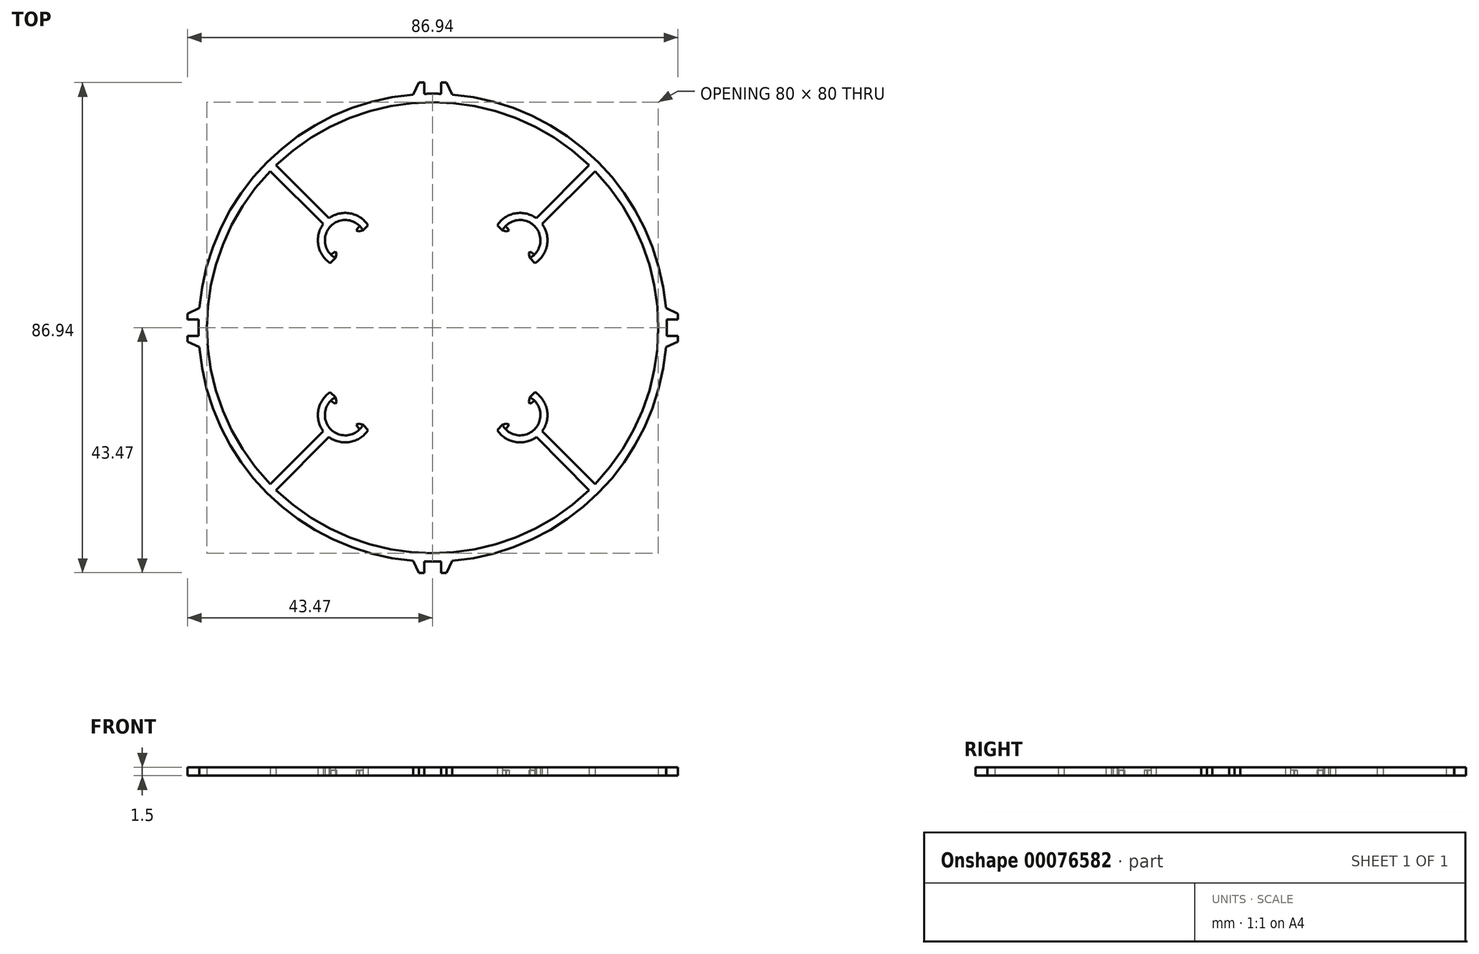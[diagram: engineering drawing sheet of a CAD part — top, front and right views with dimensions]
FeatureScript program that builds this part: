
annotation { "Feature Type Name" : "Feature", "Feature Type Description" : "" }
export const myFeature = defineFeature(function(context is Context, id is Id, definition is map)
    precondition{}
    {
        {
            var Q0;
            Q0=qCreatedBy(makeId("Top.planeOp"),FACE);
            var sketch = newSketch(context, id + "F0", { "sketchPlane" : qUnion([Q0])});
            skLineSegment(sketch, "E0.bottom", {"start": v(-15.5, 15.5) * mm, "end": v(15.5, 15.5) * mm});
            skLineSegment(sketch, "E0.top", {"start": v(-15.5, -15.5) * mm, "end": v(15.5, -15.5) * mm});
            skLineSegment(sketch, "E0.left", {"start": v(-15.5, 15.5) * mm, "end": v(-15.5, -15.5) * mm});
            skLineSegment(sketch, "E0.right", {"start": v(15.5, 15.5) * mm, "end": v(15.5, -15.5) * mm});
            skPoint(sketch, "E0.middle", {"position": v(0, 0) * mm});
            skCircle(sketch, "E1", {"center": v(-15.5, 15.5) * mm, "radius": 15 * mm});
            skCircle(sketch, "E2", {"center": v(15.5, 15.5) * mm, "radius": 15 * mm});
            skCircle(sketch, "E3", {"center": v(-15.5, -15.5) * mm, "radius": 15 * mm});
            skCircle(sketch, "E4", {"center": v(15.5, -15.5) * mm, "radius": 15 * mm});
            skLineSegment(sketch, "E5.bottom", {"start": v(-10, 10) * mm, "end": v(10, 10) * mm});
            skLineSegment(sketch, "E5.top", {"start": v(-10, -10) * mm, "end": v(10, -10) * mm});
            skLineSegment(sketch, "E5.left", {"start": v(-10, 10) * mm, "end": v(-10, -10) * mm});
            skLineSegment(sketch, "E5.right", {"start": v(10, 10) * mm, "end": v(10, -10) * mm});
            skCircle(sketch, "E6", {"center": v(-15.5, 15.5) * mm, "radius": 4.5 * mm});
            skCircle(sketch, "E7", {"center": v(-15.5, 15.5) * mm, "radius": 3.5 * mm});
            skCircle(sketch, "E8", {"center": v(15.5, 15.5) * mm, "radius": 3.5 * mm});
            skCircle(sketch, "E9", {"center": v(15.5, 15.5) * mm, "radius": 4.5 * mm});
            skCircle(sketch, "E10", {"center": v(15.5, -15.5) * mm, "radius": 4.5 * mm});
            skCircle(sketch, "E11", {"center": v(15.5, -15.5) * mm, "radius": 3.5 * mm});
            skCircle(sketch, "E12", {"center": v(-15.5, -15.5) * mm, "radius": 3.5 * mm});
            skCircle(sketch, "E13", {"center": v(-15.5, -15.5) * mm, "radius": 4.5 * mm});
            skLineSegment(sketch, "E14.bottom", {"start": v(-15.5, 15.5) * mm, "end": v(-10.5, 15.5) * mm});
            skLineSegment(sketch, "E14.left", {"start": v(-15.5, 15.5) * mm, "end": v(-15.5, 20.5) * mm});
            skLineSegment(sketch, "E15", {"start": v(-12.32, 18.68) * mm, "end": v(-18.68, 12.32) * mm});
            skLineSegment(sketch, "E16", {"start": v(-17.9, 11.7) * mm, "end": v(-11.7, 17.9) * mm});
            skSolve(sketch);
        }
        {
            var Q0;
            {var subQ1=sQuery(id+"F0.wireOp",EDGE,"E0.bottom");var subQ5=sQuery(id+"F0.wireOp",EDGE,"E14.bottom");var subQ6=makeQuery(id+"F0.imprint","INTERSECT",VERTEX,{"derivedFrom":[subQ1,subQ5]});Q0=makeQuery(id+"F0.imprint","IMPRINT",FACE,{"disambiguationData":[TD([[makeQuery(id+"F0.imprint","IMPRINT",EDGE,{"disambiguationData":[TD([[subQ6,-1.0]])],"derivedFrom":subQ1}),1.0]])]});}
            var sketch = newSketch(context, id + "F1", { "sketchPlane" : qUnion([Q0])});
            skCircle(sketch, "E17", {"center": v(0, 0) * mm, "radius": 41.5 * mm});
            skLineSegment(sketch, "E18", {"start": v(-17.05, 13.08) * mm, "end": v(-17.24, 13.54) * mm});
            skLineSegment(sketch, "E19", {"start": v(-17.24, 13.54) * mm, "end": v(-18.05, 12.95) * mm});
            skLineSegment(sketch, "E20", {"start": v(-18.39, 19.4) * mm, "end": v(-27.75, 28.8) * mm});
            skLineSegment(sketch, "E21", {"start": v(-19.4, 18.39) * mm, "end": v(-28.8, 27.75) * mm});
            skLineSegment(sketch, "E22", {"start": v(-17.25, 12.35) * mm, "end": v(-17.05, 13.08) * mm});
            skArc(sketch, "E23", {"start": v(-11.44, 18.16) * mm, "mid": v(-14.65, 20.27) * mm, "end": v(-18.39, 19.4) * mm});
            skArc(sketch, "E24", {"start": v(-12.95, 18.05) * mm, "mid": v(-18.05, 18.05) * mm, "end": v(-18.05, 12.95) * mm});
            skLineSegment(sketch, "E25.0", {"start": v(-17.9, 11.7) * mm, "end": v(-11.7, 17.9) * mm, "construction": true});
            skLineSegment(sketch, "E26", {"start": v(-12.95, 18.05) * mm, "end": v(-13.54, 17.24) * mm});
            skLineSegment(sketch, "E27", {"start": v(-13.54, 17.24) * mm, "end": v(-13.08, 17.05) * mm});
            skLineSegment(sketch, "E28", {"start": v(-13.08, 17.05) * mm, "end": v(-12.35, 17.25) * mm});
            skLineSegment(sketch, "E29", {"start": v(-12.35, 17.25) * mm, "end": v(-11.7, 17.9) * mm, "construction": true});
            skArc(sketch, "E30", {"start": v(-28.8, 27.75) * mm, "mid": v(-40, 0) * mm, "end": v(-28.8, -27.75) * mm});
            skLineSegment(sketch, "E31", {"start": v(-12.35, 17.25) * mm, "end": v(-11.44, 18.16) * mm});
            skLineSegment(sketch, "E32", {"start": v(-18.16, 11.44) * mm, "end": v(-17.25, 12.35) * mm});
            skArc(sketch, "E33.trimOffspring", {"start": v(-19.4, 18.39) * mm, "mid": v(-20.27, 14.65) * mm, "end": v(-18.16, 11.44) * mm});
            skArc(sketch, "E34.1.0", {"start": v(-18.39, -19.4) * mm, "mid": v(-14.65, -20.27) * mm, "end": v(-11.44, -18.16) * mm});
            skLineSegment(sketch, "E34.1.1", {"start": v(-19.4, -18.39) * mm, "end": v(-28.8, -27.75) * mm});
            skArc(sketch, "E34.1.2", {"start": v(-18.05, -12.95) * mm, "mid": v(-18.05, -18.05) * mm, "end": v(-12.95, -18.05) * mm});
            skLineSegment(sketch, "E34.1.3", {"start": v(-11.7, -17.9) * mm, "end": v(-17.9, -11.7) * mm, "construction": true});
            skArc(sketch, "E34.1.4", {"start": v(-18.16, -11.44) * mm, "mid": v(-20.27, -14.65) * mm, "end": v(-19.4, -18.39) * mm});
            skLineSegment(sketch, "E34.1.5", {"start": v(-18.39, -19.4) * mm, "end": v(-27.75, -28.8) * mm});
            skLineSegment(sketch, "E34.1.6", {"start": v(-18.05, -12.95) * mm, "end": v(-17.24, -13.54) * mm});
            skLineSegment(sketch, "E34.1.7", {"start": v(-13.54, -17.24) * mm, "end": v(-12.95, -18.05) * mm});
            skLineSegment(sketch, "E34.1.8", {"start": v(-17.05, -13.08) * mm, "end": v(-17.25, -12.35) * mm});
            skLineSegment(sketch, "E34.1.9", {"start": v(-17.24, -13.54) * mm, "end": v(-17.05, -13.08) * mm});
            skLineSegment(sketch, "E34.1.10", {"start": v(-11.44, -18.16) * mm, "end": v(-12.35, -17.25) * mm});
            skLineSegment(sketch, "E34.1.11", {"start": v(-12.35, -17.25) * mm, "end": v(-13.08, -17.05) * mm});
            skLineSegment(sketch, "E34.1.12", {"start": v(-17.25, -12.35) * mm, "end": v(-18.16, -11.44) * mm});
            skLineSegment(sketch, "E34.1.13", {"start": v(-13.08, -17.05) * mm, "end": v(-13.54, -17.24) * mm});
            skLineSegment(sketch, "E34.1.14", {"start": v(-17.25, -12.35) * mm, "end": v(-17.9, -11.7) * mm, "construction": true});
            skArc(sketch, "E34.2.0", {"start": v(19.4, -18.39) * mm, "mid": v(20.27, -14.65) * mm, "end": v(18.16, -11.44) * mm});
            skLineSegment(sketch, "E34.2.1", {"start": v(18.39, -19.4) * mm, "end": v(27.75, -28.8) * mm});
            skArc(sketch, "E34.2.2", {"start": v(12.95, -18.05) * mm, "mid": v(18.05, -18.05) * mm, "end": v(18.05, -12.95) * mm});
            skLineSegment(sketch, "E34.2.3", {"start": v(17.9, -11.7) * mm, "end": v(11.7, -17.9) * mm, "construction": true});
            skArc(sketch, "E34.2.4", {"start": v(11.44, -18.16) * mm, "mid": v(14.65, -20.27) * mm, "end": v(18.39, -19.4) * mm});
            skLineSegment(sketch, "E34.2.5", {"start": v(19.4, -18.39) * mm, "end": v(28.8, -27.75) * mm});
            skLineSegment(sketch, "E34.2.6", {"start": v(12.95, -18.05) * mm, "end": v(13.54, -17.24) * mm});
            skLineSegment(sketch, "E34.2.7", {"start": v(17.24, -13.54) * mm, "end": v(18.05, -12.95) * mm});
            skLineSegment(sketch, "E34.2.8", {"start": v(13.08, -17.05) * mm, "end": v(12.35, -17.25) * mm});
            skLineSegment(sketch, "E34.2.9", {"start": v(13.54, -17.24) * mm, "end": v(13.08, -17.05) * mm});
            skLineSegment(sketch, "E34.2.10", {"start": v(18.16, -11.44) * mm, "end": v(17.25, -12.35) * mm});
            skLineSegment(sketch, "E34.2.11", {"start": v(17.25, -12.35) * mm, "end": v(17.05, -13.08) * mm});
            skLineSegment(sketch, "E34.2.12", {"start": v(12.35, -17.25) * mm, "end": v(11.44, -18.16) * mm});
            skLineSegment(sketch, "E34.2.13", {"start": v(17.05, -13.08) * mm, "end": v(17.24, -13.54) * mm});
            skLineSegment(sketch, "E34.2.14", {"start": v(12.35, -17.25) * mm, "end": v(11.7, -17.9) * mm, "construction": true});
            skArc(sketch, "E34.3.0", {"start": v(18.39, 19.4) * mm, "mid": v(14.65, 20.27) * mm, "end": v(11.44, 18.16) * mm});
            skLineSegment(sketch, "E34.3.1", {"start": v(19.4, 18.39) * mm, "end": v(28.8, 27.75) * mm});
            skArc(sketch, "E34.3.2", {"start": v(18.05, 12.95) * mm, "mid": v(18.05, 18.05) * mm, "end": v(12.95, 18.05) * mm});
            skLineSegment(sketch, "E34.3.3", {"start": v(11.7, 17.9) * mm, "end": v(17.9, 11.7) * mm, "construction": true});
            skArc(sketch, "E34.3.4", {"start": v(18.16, 11.44) * mm, "mid": v(20.27, 14.65) * mm, "end": v(19.4, 18.39) * mm});
            skLineSegment(sketch, "E34.3.5", {"start": v(18.39, 19.4) * mm, "end": v(27.75, 28.8) * mm});
            skLineSegment(sketch, "E34.3.6", {"start": v(18.05, 12.95) * mm, "end": v(17.24, 13.54) * mm});
            skLineSegment(sketch, "E34.3.7", {"start": v(13.54, 17.24) * mm, "end": v(12.95, 18.05) * mm});
            skLineSegment(sketch, "E34.3.8", {"start": v(17.05, 13.08) * mm, "end": v(17.25, 12.35) * mm});
            skLineSegment(sketch, "E34.3.9", {"start": v(17.24, 13.54) * mm, "end": v(17.05, 13.08) * mm});
            skLineSegment(sketch, "E34.3.10", {"start": v(11.44, 18.16) * mm, "end": v(12.35, 17.25) * mm});
            skLineSegment(sketch, "E34.3.11", {"start": v(12.35, 17.25) * mm, "end": v(13.08, 17.05) * mm});
            skLineSegment(sketch, "E34.3.12", {"start": v(17.25, 12.35) * mm, "end": v(18.16, 11.44) * mm});
            skLineSegment(sketch, "E34.3.13", {"start": v(13.08, 17.05) * mm, "end": v(13.54, 17.24) * mm});
            skLineSegment(sketch, "E34.3.14", {"start": v(17.25, 12.35) * mm, "end": v(17.9, 11.7) * mm, "construction": true});
            skArc(sketch, "E35.trimOffspring", {"start": v(27.75, 28.8) * mm, "mid": v(0, 40) * mm, "end": v(-27.75, 28.8) * mm});
            skArc(sketch, "E36.trimOffspring", {"start": v(28.8, -27.75) * mm, "mid": v(40, 0) * mm, "end": v(28.8, 27.75) * mm});
            skArc(sketch, "E37.trimOffspring", {"start": v(-27.75, -28.8) * mm, "mid": v(0, -40) * mm, "end": v(27.75, -28.8) * mm});
            skSolve(sketch);
        }
        {
            var Q0;
            Q0=qCreatedBy(makeId("Top.planeOp"),FACE);
            var sketch = newSketch(context, id + "F2", { "sketchPlane" : qUnion([Q0])});
            skLineSegment(sketch, "E38", {"start": v(-1.47, 43.47) * mm, "end": v(-2.47, 43.47) * mm});
            skLineSegment(sketch, "E39", {"start": v(-2.47, 43.47) * mm, "end": v(-3.46, 41.36) * mm});
            skLineSegment(sketch, "E40.MirrorCS", {"start": v(1.47, 43.47) * mm, "end": v(2.47, 43.47) * mm});
            skLineSegment(sketch, "E41.MirrorCS", {"start": v(2.47, 43.47) * mm, "end": v(3.46, 41.36) * mm});
            skLineSegment(sketch, "E42", {"start": v(-1.47, 43.47) * mm, "end": v(-1.47, 41.47) * mm});
            skLineSegment(sketch, "E43", {"start": v(1.47, 43.47) * mm, "end": v(1.47, 41.47) * mm});
            skLineSegment(sketch, "E44.1.0", {"start": v(-43.47, 1.47) * mm, "end": v(-43.47, 2.47) * mm});
            skLineSegment(sketch, "E44.1.1", {"start": v(-43.47, -1.47) * mm, "end": v(-43.47, -2.47) * mm});
            skLineSegment(sketch, "E44.1.2", {"start": v(-43.47, 2.47) * mm, "end": v(-41.36, 3.46) * mm});
            skLineSegment(sketch, "E44.1.3", {"start": v(-43.47, -2.47) * mm, "end": v(-41.36, -3.46) * mm});
            skLineSegment(sketch, "E44.1.4", {"start": v(-43.47, 1.47) * mm, "end": v(-41.47, 1.47) * mm});
            skLineSegment(sketch, "E44.1.5", {"start": v(-43.47, -1.47) * mm, "end": v(-41.47, -1.47) * mm});
            skLineSegment(sketch, "E44.2.0", {"start": v(-1.47, -43.47) * mm, "end": v(-2.47, -43.47) * mm});
            skLineSegment(sketch, "E44.2.1", {"start": v(1.47, -43.47) * mm, "end": v(2.47, -43.47) * mm});
            skLineSegment(sketch, "E44.2.2", {"start": v(-2.47, -43.47) * mm, "end": v(-3.46, -41.36) * mm});
            skLineSegment(sketch, "E44.2.3", {"start": v(2.47, -43.47) * mm, "end": v(3.46, -41.36) * mm});
            skLineSegment(sketch, "E44.2.4", {"start": v(-1.47, -43.47) * mm, "end": v(-1.47, -41.47) * mm});
            skLineSegment(sketch, "E44.2.5", {"start": v(1.47, -43.47) * mm, "end": v(1.47, -41.47) * mm});
            skLineSegment(sketch, "E44.3.0", {"start": v(43.47, -1.47) * mm, "end": v(43.47, -2.47) * mm});
            skLineSegment(sketch, "E44.3.1", {"start": v(43.47, 1.47) * mm, "end": v(43.47, 2.47) * mm});
            skLineSegment(sketch, "E44.3.2", {"start": v(43.47, -2.47) * mm, "end": v(41.36, -3.46) * mm});
            skLineSegment(sketch, "E44.3.3", {"start": v(43.47, 2.47) * mm, "end": v(41.36, 3.46) * mm});
            skLineSegment(sketch, "E44.3.4", {"start": v(43.47, -1.47) * mm, "end": v(41.47, -1.47) * mm});
            skLineSegment(sketch, "E44.3.5", {"start": v(43.47, 1.47) * mm, "end": v(41.47, 1.47) * mm});
            skPoint(sketch, "E44.center", {"position": v(0, 0) * mm});
            skLineSegment(sketch, "E45", {"start": v(-41.47, 1.47) * mm, "end": v(-41.36, 3.46) * mm});
            skLineSegment(sketch, "E46", {"start": v(-41.36, -3.46) * mm, "end": v(-41.47, -1.47) * mm});
            skLineSegment(sketch, "E47", {"start": v(-3.46, 41.36) * mm, "end": v(-1.47, 41.47) * mm});
            skLineSegment(sketch, "E48", {"start": v(1.47, 41.47) * mm, "end": v(3.46, 41.36) * mm});
            skLineSegment(sketch, "E49", {"start": v(41.36, 3.46) * mm, "end": v(41.47, 1.47) * mm});
            skLineSegment(sketch, "E50", {"start": v(41.47, -1.47) * mm, "end": v(41.36, -3.46) * mm});
            skLineSegment(sketch, "E51", {"start": v(1.47, -41.47) * mm, "end": v(3.46, -41.36) * mm});
            skLineSegment(sketch, "E52", {"start": v(-1.47, -41.47) * mm, "end": v(-3.46, -41.36) * mm});
            skSolve(sketch);
        }
        {
            var Q0;
            Q0 = qSketchRegion(id + "F1", true);
            extrude(context, id + "F3", {"entities" : qUnion([Q0]), "depth" : 1.5 * mm});
        }
        {
            var Q0;
            Q0 = qSketchRegion(id + "F2", true);
            extrude(context, id + "F4", {"entities" : qUnion([Q0]), "operationType" : NewBodyOperationType.ADD, "depth" : 1.5 * mm});
        }
        {
            var Q0;
            Q0=makeQuery(id+"F4.boolean.opBoolean","MERGE",FACE,{"derivedFrom":[makeQuery(id+"F3.opExtrude","CAP_FACE",FACE,{"disambiguationData":[OSD([sQuery(id+"F1.wireOp",EDGE,"E17"),sQuery(id+"F1.wireOp",EDGE,"E18"),sQuery(id+"F1.wireOp",EDGE,"E19"),sQuery(id+"F1.wireOp",EDGE,"E20"),sQuery(id+"F1.wireOp",EDGE,"E21"),sQuery(id+"F1.wireOp",EDGE,"E22"),sQuery(id+"F1.wireOp",EDGE,"E23"),sQuery(id+"F1.wireOp",EDGE,"E24"),sQuery(id+"F1.wireOp",EDGE,"E26"),sQuery(id+"F1.wireOp",EDGE,"E27"),sQuery(id+"F1.wireOp",EDGE,"E28"),sQuery(id+"F1.wireOp",EDGE,"E30"),sQuery(id+"F1.wireOp",EDGE,"E31"),sQuery(id+"F1.wireOp",EDGE,"E32"),sQuery(id+"F1.wireOp",EDGE,"E33.trimOffspring"),sQuery(id+"F1.wireOp",EDGE,"E34.1.0"),sQuery(id+"F1.wireOp",EDGE,"E34.1.1"),sQuery(id+"F1.wireOp",EDGE,"E34.1.2"),sQuery(id+"F1.wireOp",EDGE,"E34.1.4"),sQuery(id+"F1.wireOp",EDGE,"E34.1.5"),sQuery(id+"F1.wireOp",EDGE,"E34.1.6"),sQuery(id+"F1.wireOp",EDGE,"E34.1.7"),sQuery(id+"F1.wireOp",EDGE,"E34.1.8"),sQuery(id+"F1.wireOp",EDGE,"E34.1.9"),sQuery(id+"F1.wireOp",EDGE,"E34.1.10"),sQuery(id+"F1.wireOp",EDGE,"E34.1.11"),sQuery(id+"F1.wireOp",EDGE,"E34.1.12"),sQuery(id+"F1.wireOp",EDGE,"E34.1.13"),sQuery(id+"F1.wireOp",EDGE,"E34.2.0"),sQuery(id+"F1.wireOp",EDGE,"E34.2.1"),sQuery(id+"F1.wireOp",EDGE,"E34.2.2"),sQuery(id+"F1.wireOp",EDGE,"E34.2.4"),sQuery(id+"F1.wireOp",EDGE,"E34.2.5"),sQuery(id+"F1.wireOp",EDGE,"E34.2.6"),sQuery(id+"F1.wireOp",EDGE,"E34.2.7"),sQuery(id+"F1.wireOp",EDGE,"E34.2.8"),sQuery(id+"F1.wireOp",EDGE,"E34.2.9"),sQuery(id+"F1.wireOp",EDGE,"E34.2.10"),sQuery(id+"F1.wireOp",EDGE,"E34.2.11"),sQuery(id+"F1.wireOp",EDGE,"E34.2.12"),sQuery(id+"F1.wireOp",EDGE,"E34.2.13"),sQuery(id+"F1.wireOp",EDGE,"E34.3.0"),sQuery(id+"F1.wireOp",EDGE,"E34.3.1"),sQuery(id+"F1.wireOp",EDGE,"E34.3.2"),sQuery(id+"F1.wireOp",EDGE,"E34.3.4"),sQuery(id+"F1.wireOp",EDGE,"E34.3.5"),sQuery(id+"F1.wireOp",EDGE,"E34.3.6"),sQuery(id+"F1.wireOp",EDGE,"E34.3.7"),sQuery(id+"F1.wireOp",EDGE,"E34.3.8"),sQuery(id+"F1.wireOp",EDGE,"E34.3.9"),sQuery(id+"F1.wireOp",EDGE,"E34.3.10"),sQuery(id+"F1.wireOp",EDGE,"E34.3.11"),sQuery(id+"F1.wireOp",EDGE,"E34.3.12"),sQuery(id+"F1.wireOp",EDGE,"E34.3.13"),sQuery(id+"F1.wireOp",EDGE,"E35.trimOffspring"),sQuery(id+"F1.wireOp",EDGE,"E36.trimOffspring"),sQuery(id+"F1.wireOp",EDGE,"E37.trimOffspring")])],"isStart":false}),makeQuery(id+"F4.opExtrude","CAP_FACE",FACE,{"disambiguationData":[OSD([sQuery(id+"F2.wireOp",EDGE,"E38"),sQuery(id+"F2.wireOp",EDGE,"E39"),sQuery(id+"F2.wireOp",EDGE,"E42"),sQuery(id+"F2.wireOp",EDGE,"E47")])],"isStart":false}),makeQuery(id+"F4.opExtrude","CAP_FACE",FACE,{"disambiguationData":[OSD([sQuery(id+"F2.wireOp",EDGE,"E40.MirrorCS"),sQuery(id+"F2.wireOp",EDGE,"E41.MirrorCS"),sQuery(id+"F2.wireOp",EDGE,"E43"),sQuery(id+"F2.wireOp",EDGE,"E48")])],"isStart":false}),makeQuery(id+"F4.opExtrude","CAP_FACE",FACE,{"disambiguationData":[OSD([sQuery(id+"F2.wireOp",EDGE,"E44.1.0"),sQuery(id+"F2.wireOp",EDGE,"E44.1.2"),sQuery(id+"F2.wireOp",EDGE,"E44.1.4"),sQuery(id+"F2.wireOp",EDGE,"E45")])],"isStart":false}),makeQuery(id+"F4.opExtrude","CAP_FACE",FACE,{"disambiguationData":[OSD([sQuery(id+"F2.wireOp",EDGE,"E44.1.1"),sQuery(id+"F2.wireOp",EDGE,"E44.1.3"),sQuery(id+"F2.wireOp",EDGE,"E44.1.5"),sQuery(id+"F2.wireOp",EDGE,"E46")])],"isStart":false}),makeQuery(id+"F4.opExtrude","CAP_FACE",FACE,{"disambiguationData":[OSD([sQuery(id+"F2.wireOp",EDGE,"E44.2.0"),sQuery(id+"F2.wireOp",EDGE,"E44.2.2"),sQuery(id+"F2.wireOp",EDGE,"E44.2.4"),sQuery(id+"F2.wireOp",EDGE,"E52")])],"isStart":false}),makeQuery(id+"F4.opExtrude","CAP_FACE",FACE,{"disambiguationData":[OSD([sQuery(id+"F2.wireOp",EDGE,"E44.2.1"),sQuery(id+"F2.wireOp",EDGE,"E44.2.3"),sQuery(id+"F2.wireOp",EDGE,"E44.2.5"),sQuery(id+"F2.wireOp",EDGE,"E51")])],"isStart":false}),makeQuery(id+"F4.opExtrude","CAP_FACE",FACE,{"disambiguationData":[OSD([sQuery(id+"F2.wireOp",EDGE,"E44.3.0"),sQuery(id+"F2.wireOp",EDGE,"E44.3.2"),sQuery(id+"F2.wireOp",EDGE,"E44.3.4"),sQuery(id+"F2.wireOp",EDGE,"E50")])],"isStart":false}),makeQuery(id+"F4.opExtrude","CAP_FACE",FACE,{"disambiguationData":[OSD([sQuery(id+"F2.wireOp",EDGE,"E44.3.1"),sQuery(id+"F2.wireOp",EDGE,"E44.3.3"),sQuery(id+"F2.wireOp",EDGE,"E44.3.5"),sQuery(id+"F2.wireOp",EDGE,"E49")])],"isStart":false})]});
            var sketch = newSketch(context, id + "F5", { "sketchPlane" : qUnion([Q0])});
            skPoint(sketch, "E53.0", {"position": v(-15.5, 15.5) * mm});
            skCircle(sketch, "E54", {"center": v(-15.5, 15.5) * mm, "radius": 3.6 * mm});
            skCircle(sketch, "E55.1.0", {"center": v(-15.5, -15.5) * mm, "radius": 3.6 * mm});
            skCircle(sketch, "E55.2.0", {"center": v(15.5, -15.5) * mm, "radius": 3.6 * mm});
            skCircle(sketch, "E55.3.0", {"center": v(15.5, 15.5) * mm, "radius": 3.6 * mm});
            skPoint(sketch, "E55.center", {"position": v(0, 0) * mm});
            skSolve(sketch);
        }
        {
            var Q0;
            Q0 = qSketchRegion(id + "F5", true);
            extrude(context, id + "F6", {"entities" : qUnion([Q0]), "operationType" : NewBodyOperationType.REMOVE, "oppositeDirection" : true, "depth" : 0.5 * mm});
        }
    });
